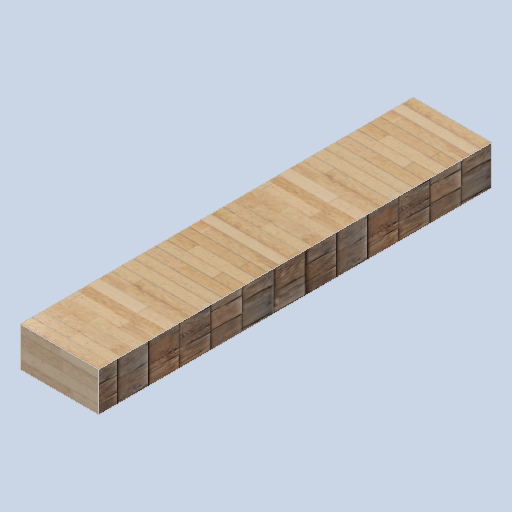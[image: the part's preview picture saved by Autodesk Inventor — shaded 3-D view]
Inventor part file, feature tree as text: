
AUTODESK INVENTOR PART (.ipt)
format: ipt  version: 2024.2 (Build 282272000, 272)  size: 375,808 bytes
history: native  units: mm
features: extrude x1, sketch x1
ambient origin geometry x8: Origin, YZ Plane, XZ Plane, XY Plane, X Axis, Y Axis, Z Axis, Center Point
bodies: Solid1 (feature_tree)
feature tree (2):
  extrude  "Extrusion1"  Depth=200.0mm
  sketch  "Sketch1"  dims[d0=400.0mm d1=200.0mm d2=2000.0mm d3=0.0mm]
